# Revit family: Data_Device-Network-Leviton-Distribution_Frame-HDX_F3168
name_source: partatom
category: Data Devices
units: mm (PartAtom-declared; Revit-internal decimal feet)

## family parameters
Classification Number = 23.85.50.17
Cut with Voids When Loaded = No
Host = Face
Maintain Annotation Orientation = Yes
Part Type = Normal
Room Calculation Point = No
Round Connector Dimension = Use Diameter
Shared = Yes

## types (1)
- F3168-22F
    Annotation Symbol is Visible = Yes
    Assembly Code = D5030600
    Check for Latest Version = http://www.leviton.com
    Date Last Modified = 2025
    Default Elevation = 0 "
    Description = HDX Fiber Distribution Frame
    Equipment Abbreviation = HDX
    Family Version = 1.0
    Manufacturer = Leviton
    Model = F3168-22F
    Model Disclaimer = http://www.leviton.com
    Part Description = HDX Fiber Distribution Frame
    Product Configurator Link = http://pct.leviton.com
    Product Documentation Link = http://www.leviton.com
    Provide Feedback = http://www.leviton.com
    URL = http://www.leviton.com
    Weight = 0.00 lb

## geometry (parser evidence)
native form markers: Blend x10, Sweep x7
no freeform markers — native parametric forms only
